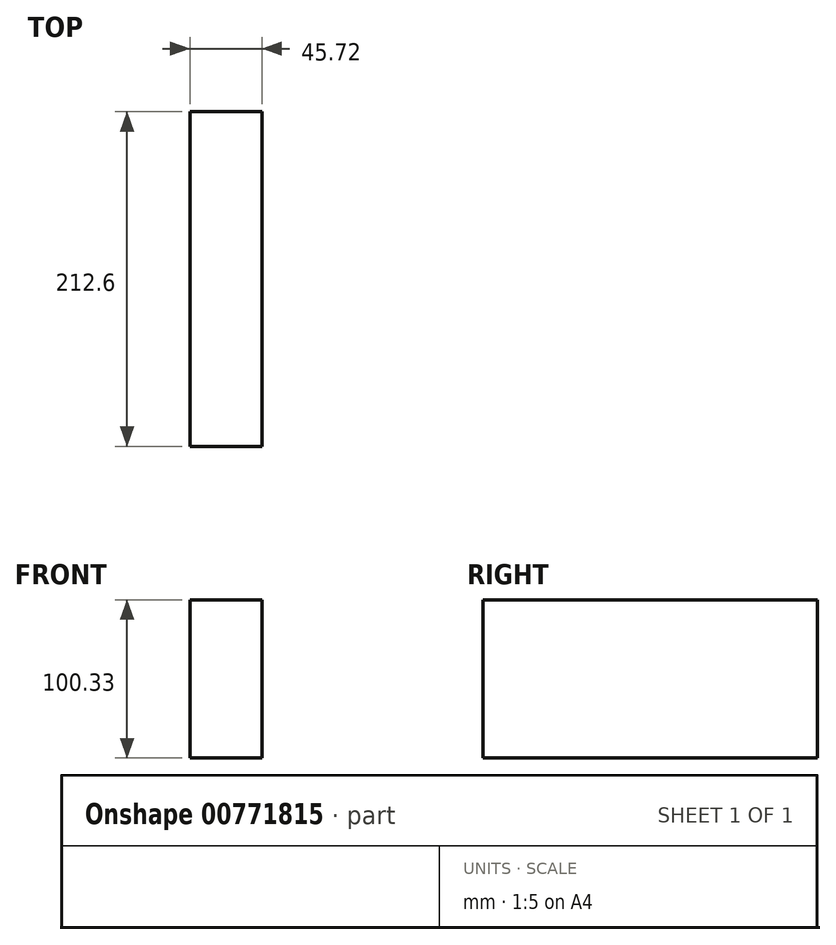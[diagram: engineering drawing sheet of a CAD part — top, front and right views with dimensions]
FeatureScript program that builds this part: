
annotation { "Feature Type Name" : "Feature", "Feature Type Description" : "" }
export const myFeature = defineFeature(function(context is Context, id is Id, definition is map)
    precondition{}
    {
        {
            var Q0;
            Q0=qCreatedBy(makeId("Front.planeOp"),FACE);
            var sketch = newSketch(context, id + "F0", { "sketchPlane" : qUnion([Q0])});
            skLineSegment(sketch, "E0", {"start": v(-45.72, 31.11) * mm, "end": v(-45.72, -69.22) * mm});
            skLineSegment(sketch, "E1", {"start": v(-45.72, 31.11) * mm, "end": v(0, 31.11) * mm});
            skLineSegment(sketch, "E2", {"start": v(0, 31.11) * mm, "end": v(0, -69.22) * mm});
            skLineSegment(sketch, "E3", {"start": v(0, -69.22) * mm, "end": v(-45.72, -69.22) * mm});
            skSolve(sketch);
        }
        {
            var Q0;
            Q0 = qSketchRegion(id + "F0", true);
            extrude(context, id + "F1", {"entities" : qUnion([Q0]), "depth" : 212.6 * mm, "offsetDistance" : 25.4 * mm});
        }
    });
